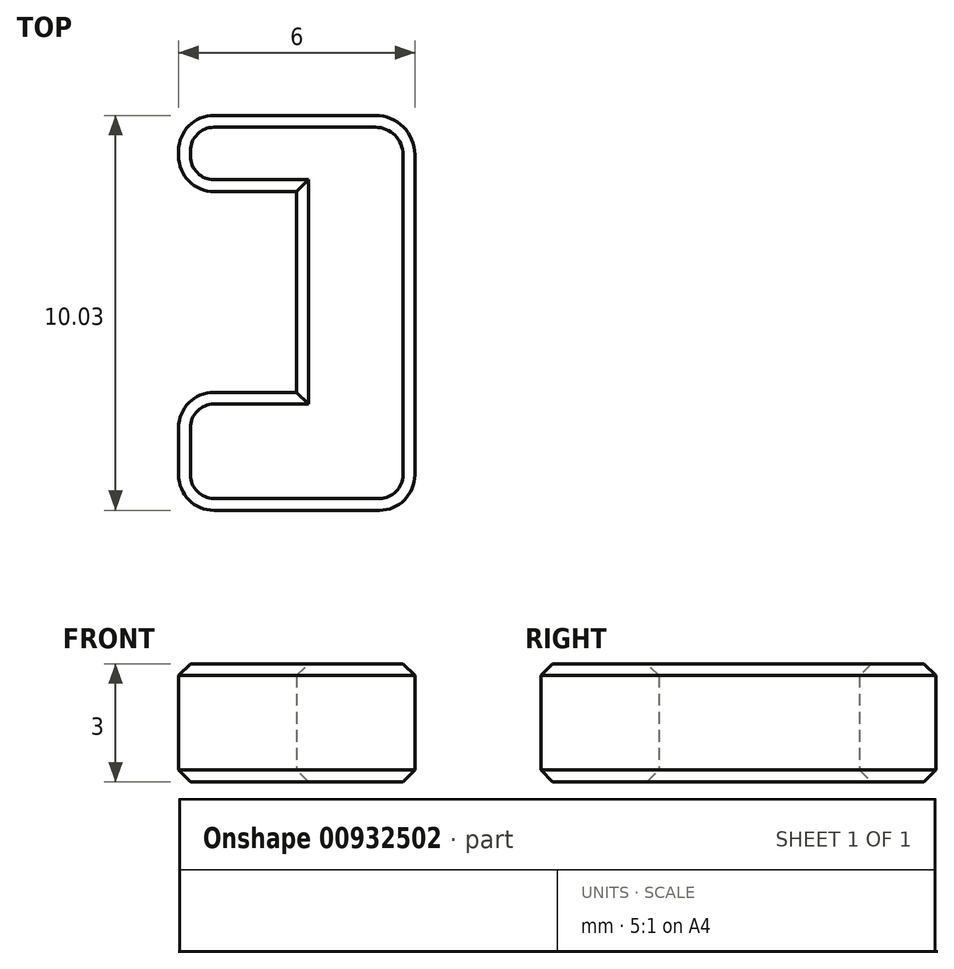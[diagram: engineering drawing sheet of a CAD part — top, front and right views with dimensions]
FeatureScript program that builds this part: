
annotation { "Feature Type Name" : "Feature", "Feature Type Description" : "" }
export const myFeature = defineFeature(function(context is Context, id is Id, definition is map)
    precondition{}
    {
        {
            var Q0;
            Q0=qCreatedBy(makeId("Top.planeOp"),FACE);
            var sketch = newSketch(context, id + "F0", { "sketchPlane" : qUnion([Q0])});
            skLineSegment(sketch, "E0", {"start": v(0.9, 8.1) * mm, "end": v(3, 8.1) * mm});
            skLineSegment(sketch, "E1", {"start": v(3, 8.1) * mm, "end": v(3, 3) * mm});
            skLineSegment(sketch, "E2", {"start": v(3, 3) * mm, "end": v(0.9, 3) * mm});
            skLineSegment(sketch, "E3", {"start": v(0, 2.1) * mm, "end": v(0, 0.9) * mm});
            skLineSegment(sketch, "E4", {"start": v(0.9, 0) * mm, "end": v(5.1, 0) * mm});
            skLineSegment(sketch, "E5", {"start": v(6, 0.9) * mm, "end": v(6, 9.03) * mm});
            skLineSegment(sketch, "E6", {"start": v(5, 10.03) * mm, "end": v(0.9, 10.03) * mm});
            skLineSegment(sketch, "E7", {"start": v(0, 9.13) * mm, "end": v(0, 9) * mm});
            skArc(sketch, "E8.filletArc", {"start": v(6, 9.03) * mm, "mid": v(5.7, 9.74) * mm, "end": v(5, 10.03) * mm});
            skPoint(sketch, "E9.visualSharp", {"position": v(6, 0) * mm});
            skArc(sketch, "E9.filletArc", {"start": v(5.1, 0) * mm, "mid": v(5.74, 0.26) * mm, "end": v(6, 0.9) * mm});
            skPoint(sketch, "E10.visualSharp", {"position": v(0, 0) * mm});
            skArc(sketch, "E10.filletArc", {"start": v(0, 0.9) * mm, "mid": v(0.26, 0.26) * mm, "end": v(0.9, 0) * mm});
            skPoint(sketch, "E11.visualSharp", {"position": v(0, 3) * mm});
            skArc(sketch, "E11.filletArc", {"start": v(0.9, 3) * mm, "mid": v(0.26, 2.74) * mm, "end": v(0, 2.1) * mm});
            skPoint(sketch, "E12.visualSharp", {"position": v(0, 10.03) * mm});
            skArc(sketch, "E12.filletArc", {"start": v(0.9, 10.03) * mm, "mid": v(0.26, 9.77) * mm, "end": v(0, 9.13) * mm});
            skPoint(sketch, "E13.visualSharp", {"position": v(0, 8.1) * mm});
            skArc(sketch, "E13.filletArc", {"start": v(0, 9) * mm, "mid": v(0.26, 8.36) * mm, "end": v(0.9, 8.1) * mm});
            skSolve(sketch);
        }
        {
            var Q0;
            Q0=makeQuery(id+"F0.imprint","IMPRINT",FACE,{"disambiguationData":[TD([[makeQuery(id+"F0.imprint","IMPRINT",EDGE,{"derivedFrom":sQuery(id+"F0.wireOp",EDGE,"E0")}),1.0]])]});
            extrude(context, id + "F1", {"entities" : qUnion([Q0]), "depth" : 3 * mm, "offsetDistance" : 25 * mm});
        }
        {
            var Q0;
            Q0=makeQuery(id+"F1.opExtrude","CAP_FACE",FACE,{"disambiguationData":[OSD([sQuery(id+"F0.wireOp",EDGE,"E0"),sQuery(id+"F0.wireOp",EDGE,"E1"),sQuery(id+"F0.wireOp",EDGE,"E2"),sQuery(id+"F0.wireOp",EDGE,"E3"),sQuery(id+"F0.wireOp",EDGE,"E4"),sQuery(id+"F0.wireOp",EDGE,"E5"),sQuery(id+"F0.wireOp",EDGE,"E6"),sQuery(id+"F0.wireOp",EDGE,"E7"),sQuery(id+"F0.wireOp",EDGE,"E8.filletArc"),sQuery(id+"F0.wireOp",EDGE,"E9.filletArc"),sQuery(id+"F0.wireOp",EDGE,"E10.filletArc"),sQuery(id+"F0.wireOp",EDGE,"E11.filletArc"),sQuery(id+"F0.wireOp",EDGE,"E12.filletArc"),sQuery(id+"F0.wireOp",EDGE,"E13.filletArc")])],"isStart":false});
            var Q1;
            Q1=makeQuery(id+"F1.opExtrude","CAP_FACE",FACE,{"disambiguationData":[OSD([sQuery(id+"F0.wireOp",EDGE,"E0"),sQuery(id+"F0.wireOp",EDGE,"E1"),sQuery(id+"F0.wireOp",EDGE,"E2"),sQuery(id+"F0.wireOp",EDGE,"E3"),sQuery(id+"F0.wireOp",EDGE,"E4"),sQuery(id+"F0.wireOp",EDGE,"E5"),sQuery(id+"F0.wireOp",EDGE,"E6"),sQuery(id+"F0.wireOp",EDGE,"E7"),sQuery(id+"F0.wireOp",EDGE,"E8.filletArc"),sQuery(id+"F0.wireOp",EDGE,"E9.filletArc"),sQuery(id+"F0.wireOp",EDGE,"E10.filletArc"),sQuery(id+"F0.wireOp",EDGE,"E11.filletArc"),sQuery(id+"F0.wireOp",EDGE,"E12.filletArc"),sQuery(id+"F0.wireOp",EDGE,"E13.filletArc")])],"isStart":true});
            chamfer(context, id + "F2", {"entities" : qUnion([Q0, Q1]), "width" : .3 * mm, "tangentPropagation" : true});
        }
    });
